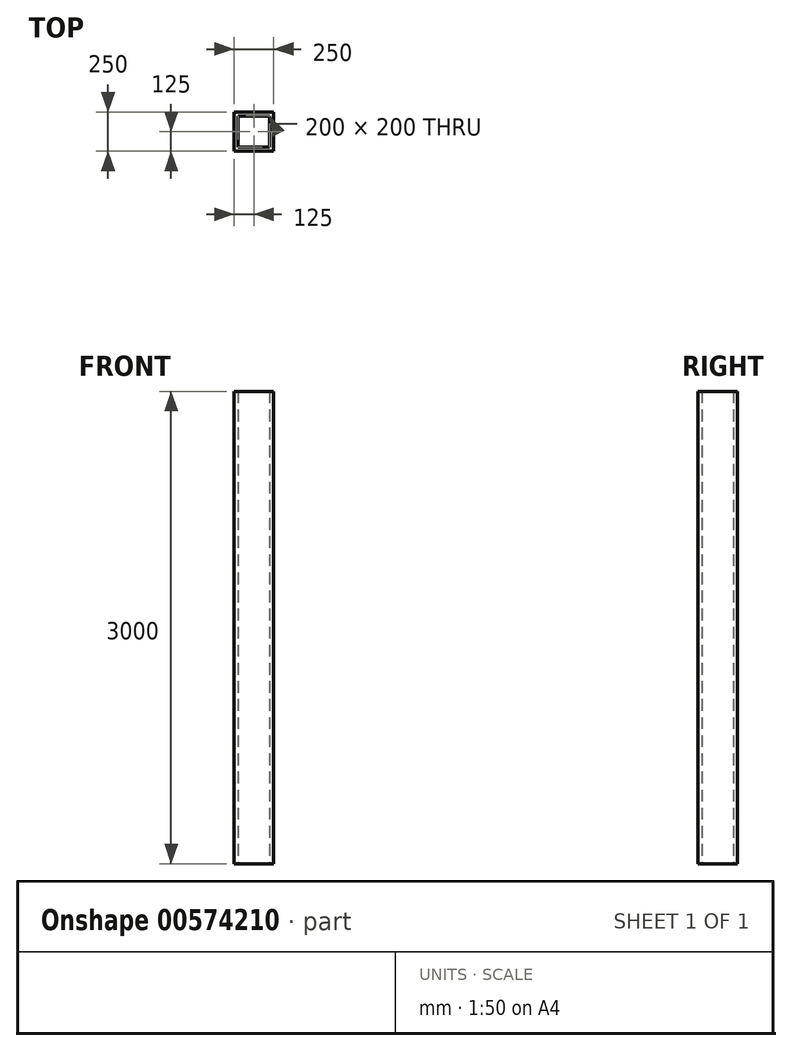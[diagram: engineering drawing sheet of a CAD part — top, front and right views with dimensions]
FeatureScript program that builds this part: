
annotation { "Feature Type Name" : "Feature", "Feature Type Description" : "" }
export const myFeature = defineFeature(function(context is Context, id is Id, definition is map)
    precondition{}
    {
        {
            var Q0;
            Q0=qCreatedBy(makeId("Top.planeOp"),FACE);
            var sketch = newSketch(context, id + "F0", { "sketchPlane" : qUnion([Q0])});
            skLineSegment(sketch, "E0.bottom", {"start": v(0, 0) * mm, "end": v(250, 0) * mm});
            skLineSegment(sketch, "E0.top", {"start": v(0, 250) * mm, "end": v(250, 250) * mm});
            skLineSegment(sketch, "E0.left", {"start": v(0, 0) * mm, "end": v(0, 250) * mm});
            skLineSegment(sketch, "E0.right", {"start": v(250, 0) * mm, "end": v(250, 250) * mm});
            skLineSegment(sketch, "E1.0", {"start": v(225, 25) * mm, "end": v(225, 225) * mm});
            skLineSegment(sketch, "E1.1", {"start": v(25, 25) * mm, "end": v(225, 25) * mm});
            skLineSegment(sketch, "E1.2", {"start": v(25, 25) * mm, "end": v(25, 225) * mm});
            skLineSegment(sketch, "E1.3", {"start": v(25, 225) * mm, "end": v(225, 225) * mm});
            skSolve(sketch);
        }
        {
            var Q0;
            Q0=makeQuery(id+"F0.imprint","IMPRINT",FACE,{"disambiguationData":[TD([[makeQuery(id+"F0.imprint","IMPRINT",EDGE,{"derivedFrom":sQuery(id+"F0.wireOp",EDGE,"E0.bottom")}),1.0]])]});
            extrude(context, id + "F1", {"entities" : qUnion([Q0]), "depth" : 3000 * mm, "offsetDistance" : 25 * mm});
        }
    });
